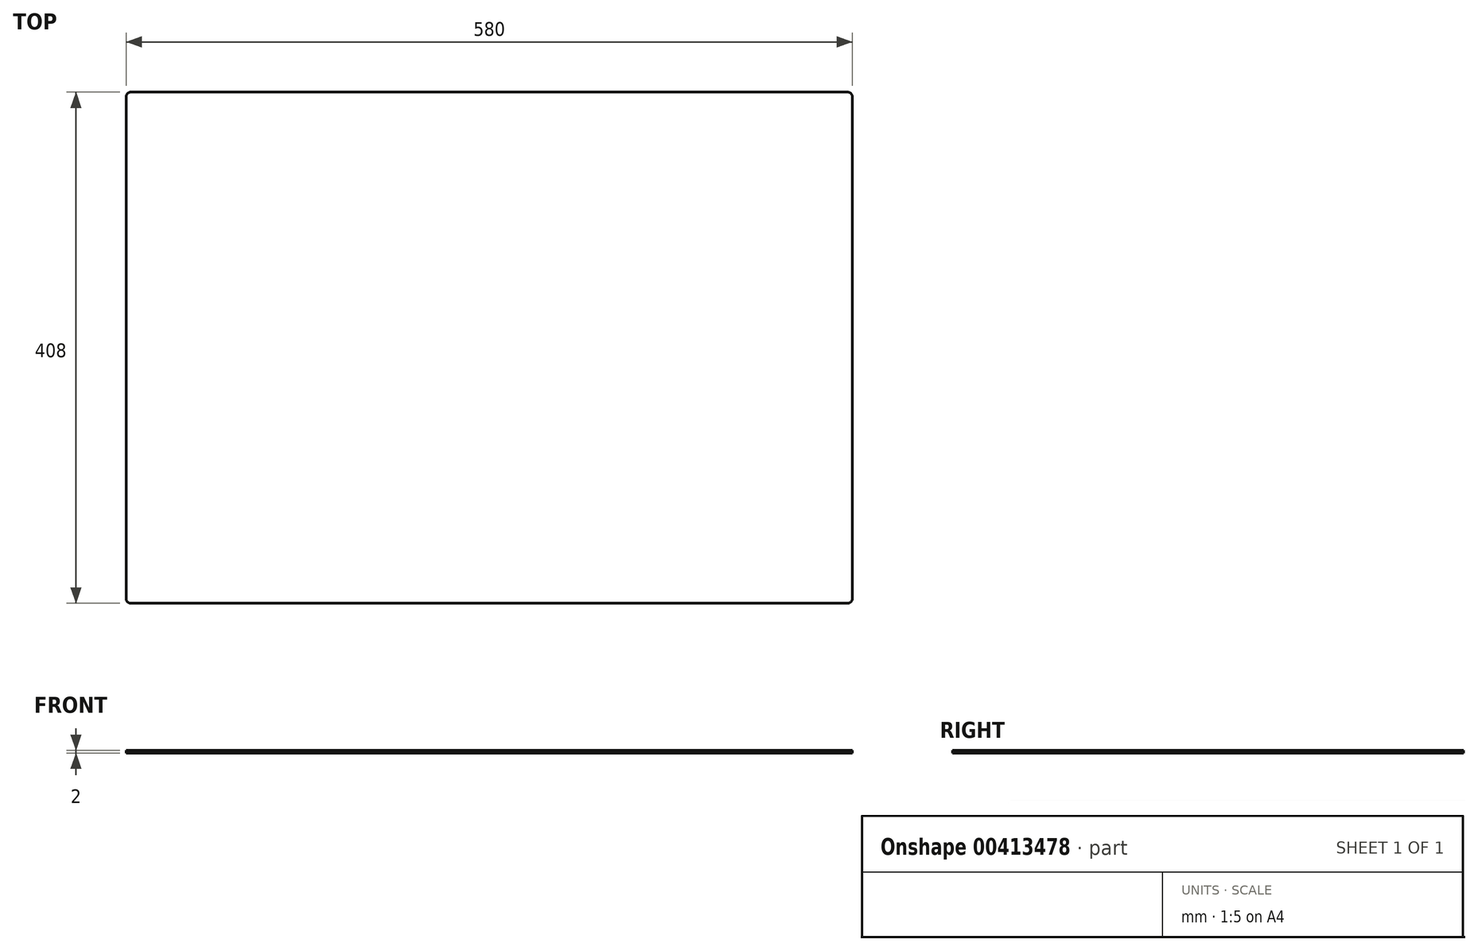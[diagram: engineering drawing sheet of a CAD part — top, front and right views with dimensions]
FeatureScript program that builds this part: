
annotation { "Feature Type Name" : "Feature", "Feature Type Description" : "" }
export const myFeature = defineFeature(function(context is Context, id is Id, definition is map)
    precondition{}
    {
        {
            var Q0;
            Q0=qCreatedBy(makeId("Top.planeOp"),FACE);
            var sketch = newSketch(context, id + "F0", { "sketchPlane" : qUnion([Q0])});
            skLineSegment(sketch, "E0.bottom", {"start": v(-286, 0) * mm, "end": v(286, 0) * mm});
            skLineSegment(sketch, "E0.top", {"start": v(-286, 408) * mm, "end": v(286, 408) * mm});
            skLineSegment(sketch, "E0.left", {"start": v(-290, 4) * mm, "end": v(-290, 404) * mm});
            skLineSegment(sketch, "E0.right", {"start": v(290, 4) * mm, "end": v(290, 404) * mm});
            skPoint(sketch, "E1.visualSharp", {"position": v(-290, 408) * mm});
            skArc(sketch, "E1.filletArc", {"start": v(-286, 408) * mm, "mid": v(-288.83, 406.83) * mm, "end": v(-290, 404) * mm});
            skPoint(sketch, "E2.visualSharp", {"position": v(290, 408) * mm});
            skArc(sketch, "E2.filletArc", {"start": v(290, 404) * mm, "mid": v(288.83, 406.83) * mm, "end": v(286, 408) * mm});
            skPoint(sketch, "E3.visualSharp", {"position": v(290, 0) * mm});
            skArc(sketch, "E3.filletArc", {"start": v(286, 0) * mm, "mid": v(288.83, 1.17) * mm, "end": v(290, 4) * mm});
            skPoint(sketch, "E4.visualSharp", {"position": v(-290, 0) * mm});
            skArc(sketch, "E4.filletArc", {"start": v(-290, 4) * mm, "mid": v(-288.83, 1.17) * mm, "end": v(-286, 0) * mm});
            skSolve(sketch);
        }
        {
            var Q0;
            Q0 = qSketchRegion(id + "F0", true);
            extrude(context, id + "F1", {"entities" : qUnion([Q0]), "depth" : 2 * mm});
        }
    });
